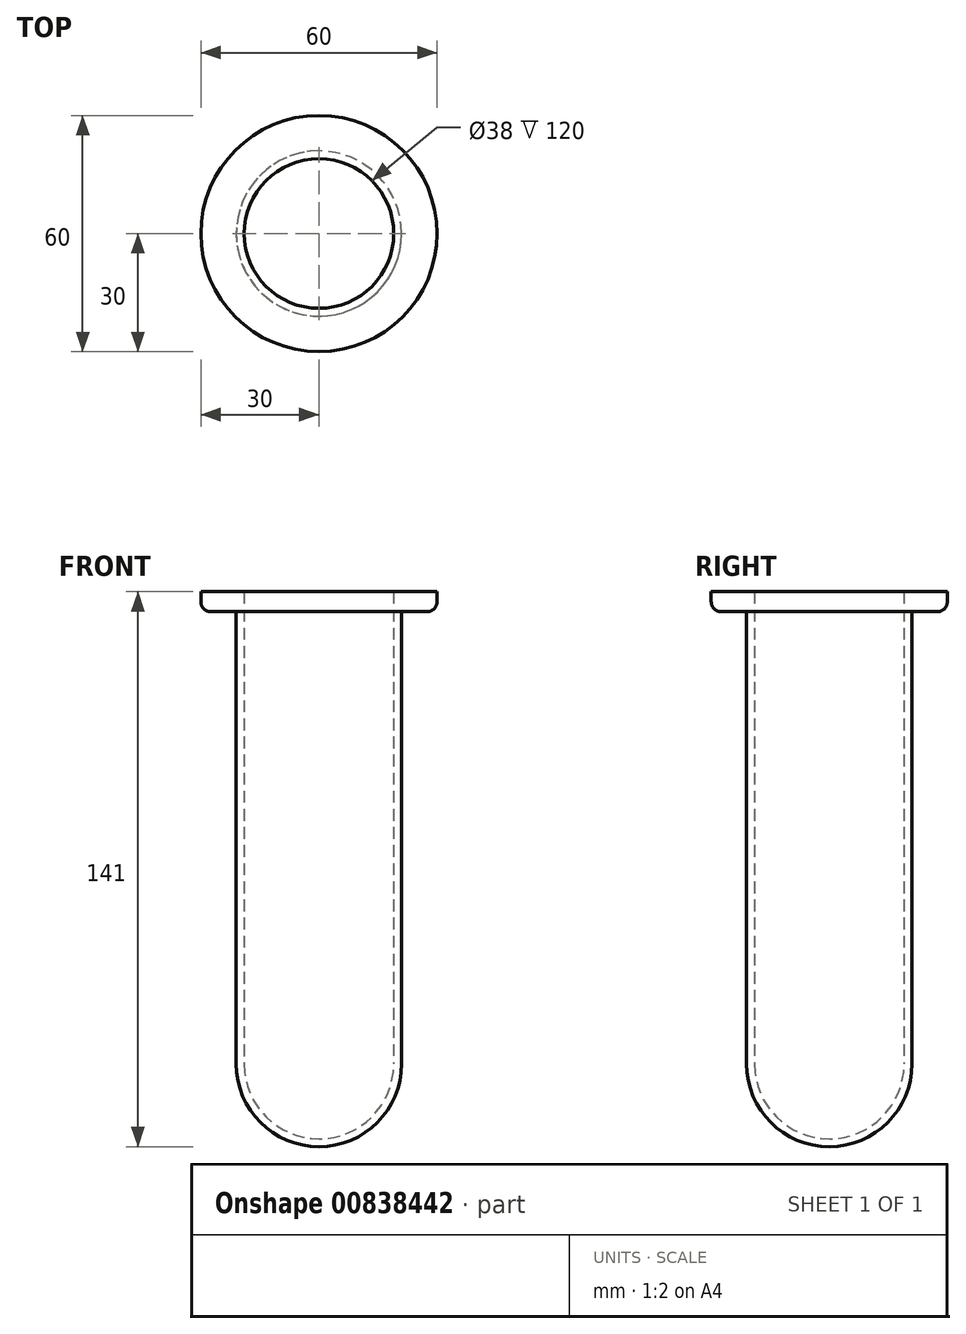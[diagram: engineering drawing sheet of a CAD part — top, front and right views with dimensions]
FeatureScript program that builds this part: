
annotation { "Feature Type Name" : "Feature", "Feature Type Description" : "" }
export const myFeature = defineFeature(function(context is Context, id is Id, definition is map)
    precondition{}
    {
        {
            var Q0;
            Q0=qCreatedBy(makeId("Top.planeOp"),FACE);
            var sketch = newSketch(context, id + "F0", { "sketchPlane" : qUnion([Q0])});
            skCircle(sketch, "E0", {"center": v(0, 0) * mm, "radius": 21 * mm});
            skLineSegment(sketch, "E1", {"start": v(0, 21) * mm, "end": v(0, -21) * mm});
            skSolve(sketch);
        }
        {
            var Q0;
            Q0=makeQuery(id+"F0.imprint","IMPRINT",FACE,{"disambiguationData":[TD([[makeQuery(id+"F0.imprint","IMPRINT",EDGE,{"derivedFrom":sQuery(id+"F0.wireOp",EDGE,"E0")}),1.0]])]});
            extrude(context, id + "F1", {"entities" : qUnion([Q0]), "depth" : 120 * mm, "offsetDistance" : 25.4 * mm});
        }
        {
            var Q0;
            Q0=makeQuery(id+"F1.opExtrude","CAP_FACE",FACE,{"disambiguationData":[OSD([sQuery(id+"F0.wireOp",EDGE,"E0")])],"isStart":false});
            shell(context, id + "F2", {"entities" : qUnion([Q0]), "thickness" : 2 * mm});
        }
        {
            var Q0;
            {var subQ0=sQuery(id+"F0.wireOp",EDGE,"E1");Q0=makeQuery(id+"F0.imprint","IMPRINT",FACE,{"disambiguationData":[TD([[makeQuery(id+"F0.imprint","IMPRINT",EDGE,{"derivedFrom":subQ0}),1.0]])]});}
            var Q1;
            Q1=sQuery(id+"F0.wireOp",EDGE,"E1");
            revolve(context, id + "F3", {"operationType" : NewBodyOperationType.ADD, "surfaceOperationType" : NewSurfaceOperationType.NEW, "entities" : qUnion([Q0]), "axis" : qUnion([Q1]), "revolveType" : RevolveType.FULL});
        }
        {
            var Q0;
            {var subQ0=sQuery(id+"F0.wireOp",EDGE,"E0");Q0=makeQuery(id+"F3.boolean.opBoolean","SPLIT",FACE,{"disambiguationData":[TD([makeQuery(id+"F2.opShell","OFFSET_FACE",FACE,{"disambiguationData":[OSD([subQ0]),TDD([makeQuery(id+"F1.opExtrude","SWEPT_FACE",FACE,{"disambiguationData":[OSD([subQ0])]})])]})])],"derivedFrom":makeQuery(id+"F3.opRevolve","SWEPT_FACE",FACE,{"disambiguationData":[OSD([subQ0])]})});}
            shell(context, id + "F4", {"entities" : qUnion([Q0]), "thickness" : 2 * mm});
        }
        {
            var Q0;
            Q0=makeQuery(id+"F1.opExtrude","CAP_FACE",FACE,{"disambiguationData":[OSD([sQuery(id+"F0.wireOp",EDGE,"E0")])],"isStart":false});
            var sketch = newSketch(context, id + "F5", { "sketchPlane" : qUnion([Q0])});
            skCircle(sketch, "E2", {"center": v(0, 0) * mm, "radius": 30 * mm});
            skSolve(sketch);
        }
        {
            var Q0;
            Q0=makeQuery(id+"F5.imprint","IMPRINT",FACE,{"disambiguationData":[TD([[makeQuery(id+"F5.imprint","IMPRINT",EDGE,{"derivedFrom":sQuery(id+"F5.wireOp",EDGE,"E2")}),1.0]])]});
            extrude(context, id + "F6", {"entities" : qUnion([Q0]), "operationType" : NewBodyOperationType.ADD, "oppositeDirection" : true, "depth" : 5.08 * mm, "offsetDistance" : 25.4 * mm});
        }
        {
            var Q0;
            Q0=makeQuery(id+"F6.opExtrude","CAP_EDGE",EDGE,{"disambiguationData":[OSD([sQuery(id+"F5.wireOp",EDGE,"E2")])],"isStart":false});
            fillet(context, id + "F7", {"entities" : qUnion([Q0]), "radius" : 2.54 * mm, "tangentPropagation" : true, "allowEdgeOverflow" : false});
        }
    });
